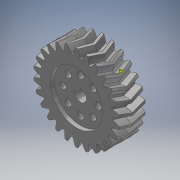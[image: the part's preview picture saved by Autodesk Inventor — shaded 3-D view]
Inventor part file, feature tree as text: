
AUTODESK INVENTOR PART (.ipt)
format: ipt  version: 2019 (Build 230136000, 136)  size: 1,241,600 bytes
history: native  units: mm (DEFAULTED — no unit token found)
features: sketch x6, extrude x3, plane x3, other x3, mirror x2, hole x2, chamfer x1
ambient origin geometry x8: Origin, YZ Plane, XZ Plane, XY Plane, X Axis, Y Axis, Z Axis, Center Point
bodies: Solid1 (feature_tree)
feature tree (20):
  extrude  "Extrusion1"  Depth=5.0mm TaperAngle=0.0deg
  plane  "Work Plane2"
  plane  "Work Plane8"
  plane  "Work Plane9"
  other  "Spur Gear"
  mirror  "Mirror1"
  extrude  "Extrusion2"  Depth=10.0mm TaperAngle=0.0deg
  hole  "Hole1"  [1 undecoded]
  hole  "Hole2"  [1 undecoded]
  extrude  "Extrusion3"  Depth=31.29mm
  chamfer  "Chamfer1"  [1 undecoded]
  mirror  "Mirror2"
  sketch  "Sketch1"  dims[d0=32.949264mm d1=5.0mm d2=0.0mm]
  sketch  "Sketch2"  dims[d3=30.699623mm d4=10.0mm d5=0.0mm]
  other  "Srf1"
  sketch  "Sketch3"  dims[d16=31.29mm d17=0.0mm d34=1.208305mm]
  sketch  "Sketch4"  dims[d39=0.0mm d41=0.0mm]
  sketch  "Sketch5"  dims[d43=31.29mm d46=31.29mm d47=0.0mm d48=0.0mm]
  sketch  "Sketch6"  dims[d49=18.0mm d50=5.0mm d51=0.0mm d52=13.5mm d53=80.0mm d55=360.0deg d57=2.5mm d58=6.0mm d59=4.0mm d60=3.0mm d61=90.0deg d62=8.0mm d63=0.0mm d64=4.5mm d65=6.0mm d66=4.0mm d67=3.0mm d68=90.0deg d69=8.0mm d70=0.0mm d71=20.0mm d72=1.55mm d73=0.0mm d74=1.5mm d75=4.0mm d76=45.0deg]
  other  "Pitch Diameter"
note: 3 required parameter values undecoded (feature->parameter linkage not recoverable at this tier; creation-order binding heuristic only, values carry confidence <= 0.55)
